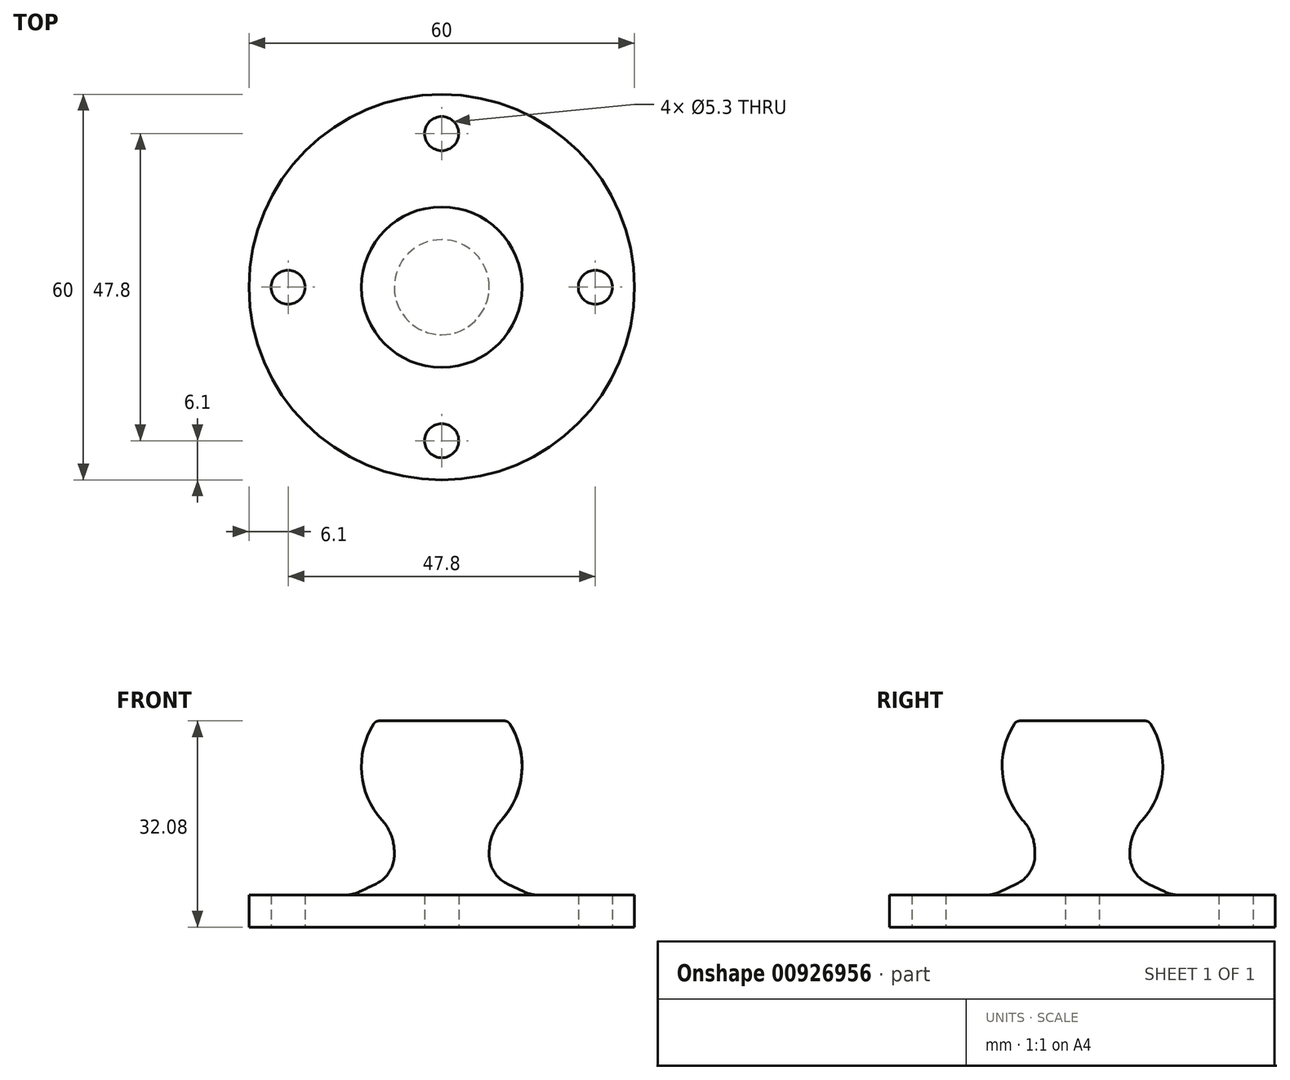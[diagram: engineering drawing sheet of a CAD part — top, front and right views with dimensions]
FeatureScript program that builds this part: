
annotation { "Feature Type Name" : "Feature", "Feature Type Description" : "" }
export const myFeature = defineFeature(function(context is Context, id is Id, definition is map)
    precondition{}
    {
        {
            var Q0;
            Q0=qCreatedBy(makeId("Front.planeOp"),FACE);
            var sketch = newSketch(context, id + "F0", { "sketchPlane" : qUnion([Q0])});
            skLineSegment(sketch, "E0", {"start": v(0, 0) * mm, "end": v(30, 0) * mm});
            skLineSegment(sketch, "E1", {"start": v(30, 0) * mm, "end": v(30, 5) * mm});
            skLineSegment(sketch, "E2", {"start": v(0, 0) * mm, "end": v(0, 25) * mm});
            skArc(sketch, "E3", {"start": v(7.39, 14.92) * mm, "mid": v(12.32, 22.9) * mm, "end": v(10.3, 32.08) * mm});
            skLineSegment(sketch, "E4", {"start": v(0, 25) * mm, "end": v(0, 32.08) * mm});
            skLineSegment(sketch, "E5", {"start": v(7.39, 14.92) * mm, "end": v(7.39, 8.07) * mm});
            skLineSegment(sketch, "E6", {"start": v(30, 5) * mm, "end": v(13.85, 5) * mm});
            skLineSegment(sketch, "E7", {"start": v(10.3, 32.08) * mm, "end": v(0, 32.08) * mm});
            skLineSegment(sketch, "E8", {"start": v(7.39, 8.07) * mm, "end": v(13.85, 5) * mm});
            skSolve(sketch);
        }
        {
            var Q0;
            Q0=makeQuery(id+"F0.imprint","IMPRINT",FACE,{"disambiguationData":[TD([[makeQuery(id+"F0.imprint","IMPRINT",EDGE,{"derivedFrom":sQuery(id+"F0.wireOp",EDGE,"E0")}),1.0]])]});
            var Q1;
            Q1=sQuery(id+"F0.wireOp",EDGE,"E2");
            revolve(context, id + "F1", {"surfaceOperationType" : NewSurfaceOperationType.NEW, "entities" : qUnion([Q0]), "axis" : qUnion([Q1]), "revolveType" : RevolveType.FULL});
        }
        {
            var Q0;
            Q0=makeQuery(id+"F1.opRevolve","SWEPT_FACE",FACE,{"disambiguationData":[OSD([sQuery(id+"F0.wireOp",EDGE,"E0")])]});
            var sketch = newSketch(context, id + "F2", { "sketchPlane" : qUnion([Q0])});
            skCircle(sketch, "E9", {"center": v(0, 0) * mm, "radius": 23.9 * mm, "construction": true});
            skLineSegment(sketch, "E10", {"start": v(0, 52.38) * mm, "end": v(0, -51.18) * mm, "construction": true});
            skLineSegment(sketch, "E11", {"start": v(52.14, 0) * mm, "end": v(-63.46, 0) * mm, "construction": true});
            skPoint(sketch, "E12", {"position": v(0, 23.9) * mm});
            skPoint(sketch, "E13", {"position": v(23.9, 0) * mm});
            skPoint(sketch, "E14", {"position": v(0, -23.9) * mm});
            skPoint(sketch, "E15", {"position": v(-23.9, 0) * mm});
            skCircle(sketch, "E16", {"center": v(0, 23.9) * mm, "radius": 2.65 * mm});
            skCircle(sketch, "E17", {"center": v(23.9, 0) * mm, "radius": 2.65 * mm});
            skCircle(sketch, "E18", {"center": v(0, -23.9) * mm, "radius": 2.65 * mm});
            skCircle(sketch, "E19", {"center": v(-23.9, 0) * mm, "radius": 2.65 * mm});
            skSolve(sketch);
        }
        {
            var Q0;
            Q0 = qSketchRegion(id + "F2", true);
            extrude(context, id + "F3", {"entities" : qUnion([Q0]), "operationType" : NewBodyOperationType.REMOVE, "oppositeDirection" : true, "depth" : 25 * mm, "offsetDistance" : 25 * mm});
        }
        {
            var Q0;
            Q0=makeQuery(id+"F1.opRevolve","SWEPT_EDGE",EDGE,{"disambiguationData":[OSD([sQuery(id+"F0.wireOp",EDGE,"E3"),sQuery(id+"F0.wireOp",EDGE,"E5")])]});
            fillet(context, id + "F4", {"entities" : qUnion([Q0]), "radius" : 7.43 * mm, "tangentPropagation" : true, "allowEdgeOverflow" : false});
        }
        {
            var Q0;
            Q0=makeQuery(id+"F1.opRevolve","SWEPT_EDGE",EDGE,{"disambiguationData":[OSD([sQuery(id+"F0.wireOp",EDGE,"E5"),sQuery(id+"F0.wireOp",EDGE,"E8")])]});
            var Q1;
            Q1=makeQuery(id+"F1.opRevolve","SWEPT_EDGE",EDGE,{"disambiguationData":[OSD([sQuery(id+"F0.wireOp",EDGE,"E6"),sQuery(id+"F0.wireOp",EDGE,"E8")])]});
            fillet(context, id + "F5", {"entities" : qUnion([Q0, Q1]), "radius" : 5 * mm, "tangentPropagation" : true, "allowEdgeOverflow" : false});
        }
        {
            var Q0;
            Q0=makeQuery(id+"F1.opRevolve","SWEPT_EDGE",EDGE,{"disambiguationData":[OSD([sQuery(id+"F0.wireOp",EDGE,"E3"),sQuery(id+"F0.wireOp",EDGE,"E7")])]});
            fillet(context, id + "F6", {"entities" : qUnion([Q0]), "radius" : 1 * mm, "tangentPropagation" : true, "allowEdgeOverflow" : false});
        }
    });
